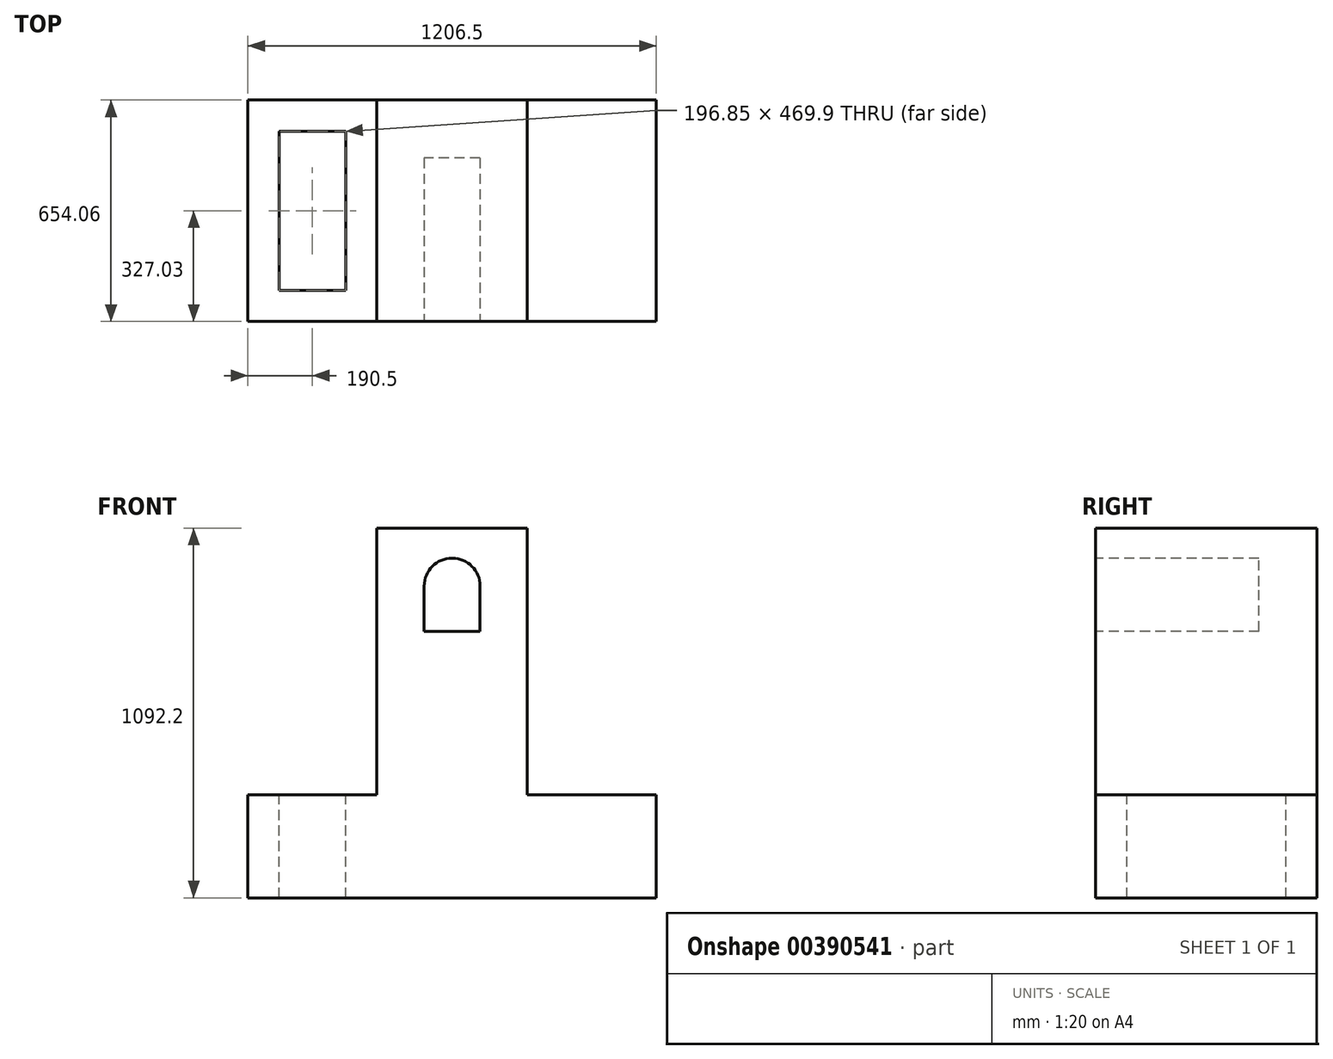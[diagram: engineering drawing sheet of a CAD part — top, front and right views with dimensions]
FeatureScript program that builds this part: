
annotation { "Feature Type Name" : "Feature", "Feature Type Description" : "" }
export const myFeature = defineFeature(function(context is Context, id is Id, definition is map)
    precondition{}
    {
        {
            var Q0;
            Q0=qCreatedBy(makeId("Top.planeOp"),FACE);
            var sketch = newSketch(context, id + "F0", { "sketchPlane" : qUnion([Q0])});
            skLineSegment(sketch, "E0.bottom", {"start": v(222.25, -327.03) * mm, "end": v(-222.25, -327.03) * mm});
            skLineSegment(sketch, "E0.top", {"start": v(222.25, 327.03) * mm, "end": v(-222.25, 327.03) * mm});
            skLineSegment(sketch, "E0.left", {"start": v(222.25, -327.03) * mm, "end": v(222.25, 327.03) * mm});
            skLineSegment(sketch, "E0.right", {"start": v(-222.25, -327.03) * mm, "end": v(-222.25, 327.03) * mm});
            skPoint(sketch, "E0.middle", {"position": v(0, 0) * mm});
            skSolve(sketch);
        }
        {
            var Q0;
            Q0=makeQuery(id+"F0.imprint","IMPRINT",FACE,{"disambiguationData":[TD([[makeQuery(id+"F0.imprint","IMPRINT",EDGE,{"derivedFrom":sQuery(id+"F0.wireOp",EDGE,"E0.bottom")}),-1.0]])]});
            var Q1;
            Q1=sQuery(id+"F0.wireOp",EDGE,"E0.left");
            var Q2;
            Q2=sQuery(id+"F0.wireOp",EDGE,"E0.bottom");
            var Q3;
            Q3=sQuery(id+"F0.wireOp",EDGE,"E0.right");
            var Q4;
            Q4=sQuery(id+"F0.wireOp",EDGE,"E0.top");
            extrude(context, id + "F1", {"entities" : qUnion([Q0]), "surfaceEntities" : qUnion([Q1, Q2, Q3, Q4]), "depth" : 1092.2 * mm});
        }
        {
            var Q0;
            Q0=makeQuery(id+"F1.opExtrude","SWEPT_FACE",FACE,{"disambiguationData":[OSD([sQuery(id+"F0.wireOp",EDGE,"E0.bottom")])]});
            var sketch = newSketch(context, id + "F2", { "sketchPlane" : qUnion([Q0])});
            skLineSegment(sketch, "E1.bottom", {"start": v(222.25, 0) * mm, "end": v(603.25, 0) * mm});
            skLineSegment(sketch, "E1.top", {"start": v(222.25, 304.8) * mm, "end": v(603.25, 304.8) * mm});
            skLineSegment(sketch, "E1.left", {"start": v(222.25, 0) * mm, "end": v(222.25, 304.8) * mm});
            skLineSegment(sketch, "E1.right", {"start": v(603.25, 0) * mm, "end": v(603.25, 304.8) * mm});
            skLineSegment(sketch, "E2.bottom", {"start": v(-222.25, 0) * mm, "end": v(-603.25, 0) * mm});
            skLineSegment(sketch, "E2.top", {"start": v(-222.25, 304.8) * mm, "end": v(-603.25, 304.8) * mm});
            skLineSegment(sketch, "E2.left", {"start": v(-222.25, 0) * mm, "end": v(-222.25, 304.8) * mm});
            skLineSegment(sketch, "E2.right", {"start": v(-603.25, 0) * mm, "end": v(-603.25, 304.8) * mm});
            skSolve(sketch);
        }
        {
            var Q0;
            Q0 = qSketchRegion(id + "F2", true);
            var Q1;
            Q1=makeQuery(id+"F1.opExtrude","SWEPT_FACE",FACE,{"disambiguationData":[OSD([sQuery(id+"F0.wireOp",EDGE,"E0.top")])]});
            extrude(context, id + "F3", {"entities" : qUnion([Q0]), "operationType" : NewBodyOperationType.ADD, "endBound" : BoundingType.UP_TO_SURFACE, "oppositeDirection" : true, "endBoundEntityFace" : qUnion([Q1]), "depth" : 25.4 * mm});
        }
        {
            var Q0;
            Q0=makeQuery(id+"F3.opExtrude","SWEPT_FACE",FACE,{"disambiguationData":[OSD([sQuery(id+"F2.wireOp",EDGE,"E2.top")])]});
            var sketch = newSketch(context, id + "F4", { "sketchPlane" : qUnion([Q0])});
            skLineSegment(sketch, "E3", {"start": v(-222.25, 327.02) * mm, "end": v(-603.25, -327.03) * mm});
            skLineSegment(sketch, "E4.bottom", {"start": v(-314.33, 234.95) * mm, "end": v(-511.18, 234.95) * mm});
            skLineSegment(sketch, "E4.top", {"start": v(-314.33, -234.95) * mm, "end": v(-511.18, -234.95) * mm});
            skLineSegment(sketch, "E4.left", {"start": v(-314.33, 234.95) * mm, "end": v(-314.33, -234.95) * mm});
            skLineSegment(sketch, "E4.right", {"start": v(-511.18, 234.95) * mm, "end": v(-511.18, -234.95) * mm});
            skPoint(sketch, "E4.middle", {"position": v(-412.75, 0) * mm});
            skSolve(sketch);
        }
        {
            var Q0;
            Q0 = qSketchRegion(id + "F4", true);
            extrude(context, id + "F5", {"entities" : qUnion([Q0]), "operationType" : NewBodyOperationType.REMOVE, "endBound" : BoundingType.THROUGH_ALL, "oppositeDirection" : true, "depth" : 25.4 * mm});
        }
        {
            var Q0;
            Q0=makeQuery(id+"F3.boolean.opBoolean","MERGE",FACE,{"derivedFrom":[makeQuery(id+"F1.opExtrude","SWEPT_FACE",FACE,{"disambiguationData":[OSD([sQuery(id+"F0.wireOp",EDGE,"E0.bottom")])]}),makeQuery(id+"F3.opExtrude","CAP_FACE",FACE,{"disambiguationData":[OSD([sQuery(id+"F2.wireOp",EDGE,"E1.bottom"),sQuery(id+"F2.wireOp",EDGE,"E1.top"),sQuery(id+"F2.wireOp",EDGE,"E1.left"),sQuery(id+"F2.wireOp",EDGE,"E1.right")])],"isStart":true}),makeQuery(id+"F3.opExtrude","CAP_FACE",FACE,{"disambiguationData":[OSD([sQuery(id+"F2.wireOp",EDGE,"E2.bottom"),sQuery(id+"F2.wireOp",EDGE,"E2.top"),sQuery(id+"F2.wireOp",EDGE,"E2.left"),sQuery(id+"F2.wireOp",EDGE,"E2.right")])],"isStart":true})]});
            var sketch = newSketch(context, id + "F6", { "sketchPlane" : qUnion([Q0])});
            skLineSegment(sketch, "E5", {"start": v(0, 1092.2) * mm, "end": v(0, 0) * mm});
            skLineSegment(sketch, "E6.bottom", {"start": v(82.55, 787.4) * mm, "end": v(-82.55, 787.4) * mm});
            skLineSegment(sketch, "E6.top", {"start": v(82.55, 920.75) * mm, "end": v(-82.55, 920.75) * mm});
            skLineSegment(sketch, "E6.left", {"start": v(82.55, 787.4) * mm, "end": v(82.55, 920.75) * mm});
            skLineSegment(sketch, "E6.right", {"start": v(-82.55, 787.4) * mm, "end": v(-82.55, 920.75) * mm});
            skPoint(sketch, "E6.middle", {"position": v(0, 854.08) * mm});
            skCircle(sketch, "E7", {"center": v(0, 920.75) * mm, "radius": 82.55 * mm});
            skSolve(sketch);
        }
        {
            var Q0;
            Q0 = qSketchRegion(id + "F6", true);
            extrude(context, id + "F7", {"entities" : qUnion([Q0]), "operationType" : NewBodyOperationType.REMOVE, "oppositeDirection" : true, "depth" : 482.6 * mm});
        }
    });
